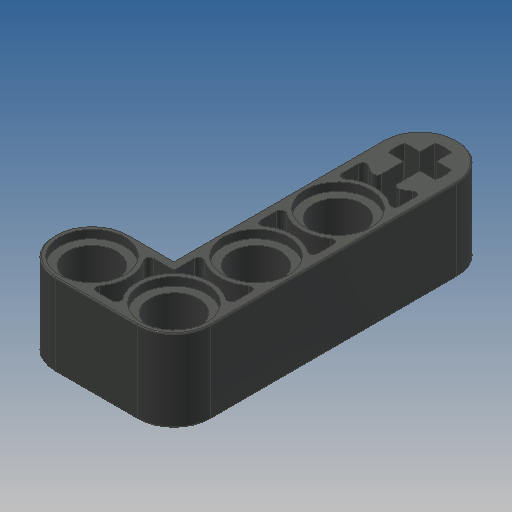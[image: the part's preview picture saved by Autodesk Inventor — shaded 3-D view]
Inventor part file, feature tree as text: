
AUTODESK INVENTOR PART (.ipt)
format: ipt  version: 2022.2 (Build 262287000, 287)  size: 316,928 bytes
history: native  units: mm
features: extrude x3, sketch x2, mirror x1, fillet x1
ambient origin geometry x8: Origin, YZ Plane, XZ Plane, XY Plane, X Axis, Y Axis, Z Axis, Center Point
bodies: Solid1 (feature_tree)
feature tree (7):
  extrude  "Extrusion1"  Depth=6.4mm
  sketch  "Sketch6"  dims[d14=8.0mm d15=0.0mm d32=7.2mm d34=8.0mm d36=0.8mm d41=0.8mm d42=0.0mm d43=3.1mm d44=0.0mm d46=0.4mm d47=0.1mm d48=1.6mm d49=0.8mm]
  extrude  "Extrusion7"  Depth=7.2mm
  extrude  "Extrusion8"  Depth=8.0mm
  mirror  "Mirror1"
  fillet  "Fillet1"  Radius=0.8mm
  sketch  "Sketch1"  dims[d8=4.8mm d9=6.4mm]
